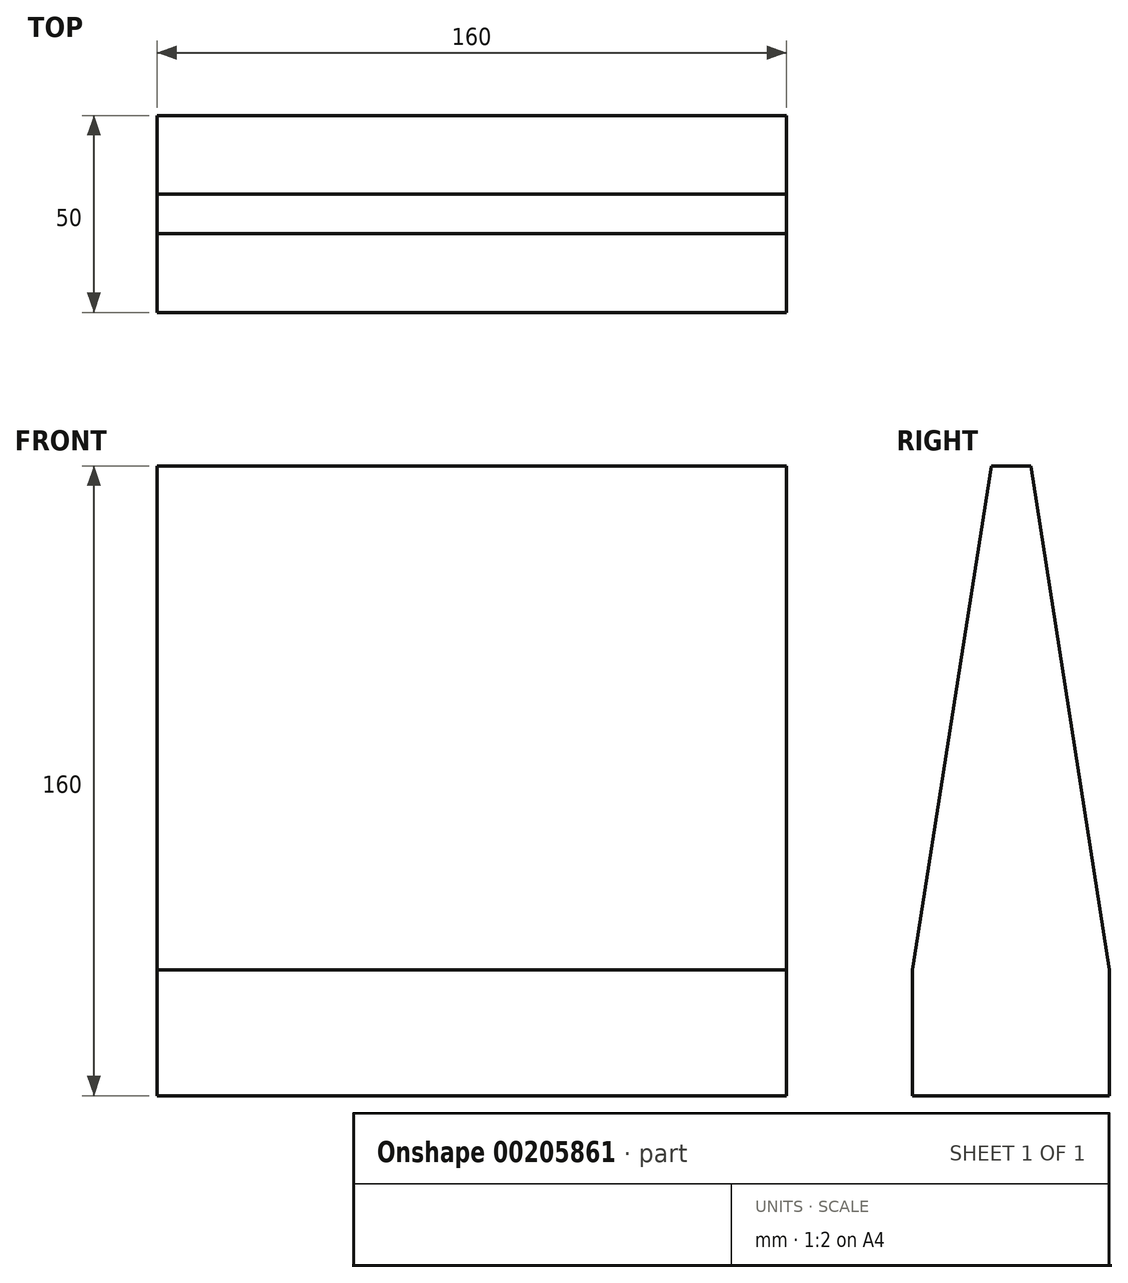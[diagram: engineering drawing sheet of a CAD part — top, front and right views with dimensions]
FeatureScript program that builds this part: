
annotation { "Feature Type Name" : "Feature", "Feature Type Description" : "" }
export const myFeature = defineFeature(function(context is Context, id is Id, definition is map)
    precondition{}
    {
        {
            var Q0;
            Q0=qCreatedBy(makeId("Top.planeOp"),FACE);
            var sketch = newSketch(context, id + "F0", { "sketchPlane" : qUnion([Q0])});
            skLineSegment(sketch, "E0.bottom", {"start": v(-80, 25) * mm, "end": v(80, 25) * mm});
            skLineSegment(sketch, "E0.top", {"start": v(-80, -25) * mm, "end": v(80, -25) * mm});
            skLineSegment(sketch, "E0.left", {"start": v(-80, 25) * mm, "end": v(-80, -25) * mm});
            skLineSegment(sketch, "E0.right", {"start": v(80, 25) * mm, "end": v(80, -25) * mm});
            skPoint(sketch, "E0.middle", {"position": v(0, 0) * mm});
            skSolve(sketch);
        }
        {
            var Q0;
            Q0=makeQuery(id+"F0.imprint","IMPRINT",FACE,{"disambiguationData":[TD([[makeQuery(id+"F0.imprint","IMPRINT",EDGE,{"derivedFrom":sQuery(id+"F0.wireOp",EDGE,"E0.bottom")}),-1.0]])]});
            extrude(context, id + "F1", {"entities" : qUnion([Q0]), "depth" : 32 * mm});
        }
        {
            var Q0;
            Q0=makeQuery(id+"F1.opExtrude","SWEPT_FACE",FACE,{"disambiguationData":[OSD([sQuery(id+"F0.wireOp",EDGE,"E0.left")])]});
            var sketch = newSketch(context, id + "F2", { "sketchPlane" : qUnion([Q0])});
            skPoint(sketch, "E1.endSnap0", {"position": v(0, 32) * mm});
            skLineSegment(sketch, "E2", {"start": v(0, 32) * mm, "end": v(0, 160) * mm, "construction": true});
            skLineSegment(sketch, "E3", {"start": v(-5, 160) * mm, "end": v(5, 160) * mm});
            skLineSegment(sketch, "E4", {"start": v(-25, 32) * mm, "end": v(-5, 160) * mm});
            skLineSegment(sketch, "E5", {"start": v(25, 32) * mm, "end": v(5, 160) * mm});
            skPoint(sketch, "E6.orphan", {"position": v(-33.13, 160) * mm});
            skSolve(sketch);
        }
        {
            var Q0;
            Q0=makeQuery(id+"F2.imprint","IMPRINT",FACE,{"disambiguationData":[TD([[makeQuery(id+"F2.imprint","IMPRINT",EDGE,{"derivedFrom":sQuery(id+"F2.wireOp",EDGE,"E3")}),-1.0]])]});
            extrude(context, id + "F3", {"entities" : qUnion([Q0]), "operationType" : NewBodyOperationType.ADD, "oppositeDirection" : true, "depth" : 160 * mm});
        }
    });
